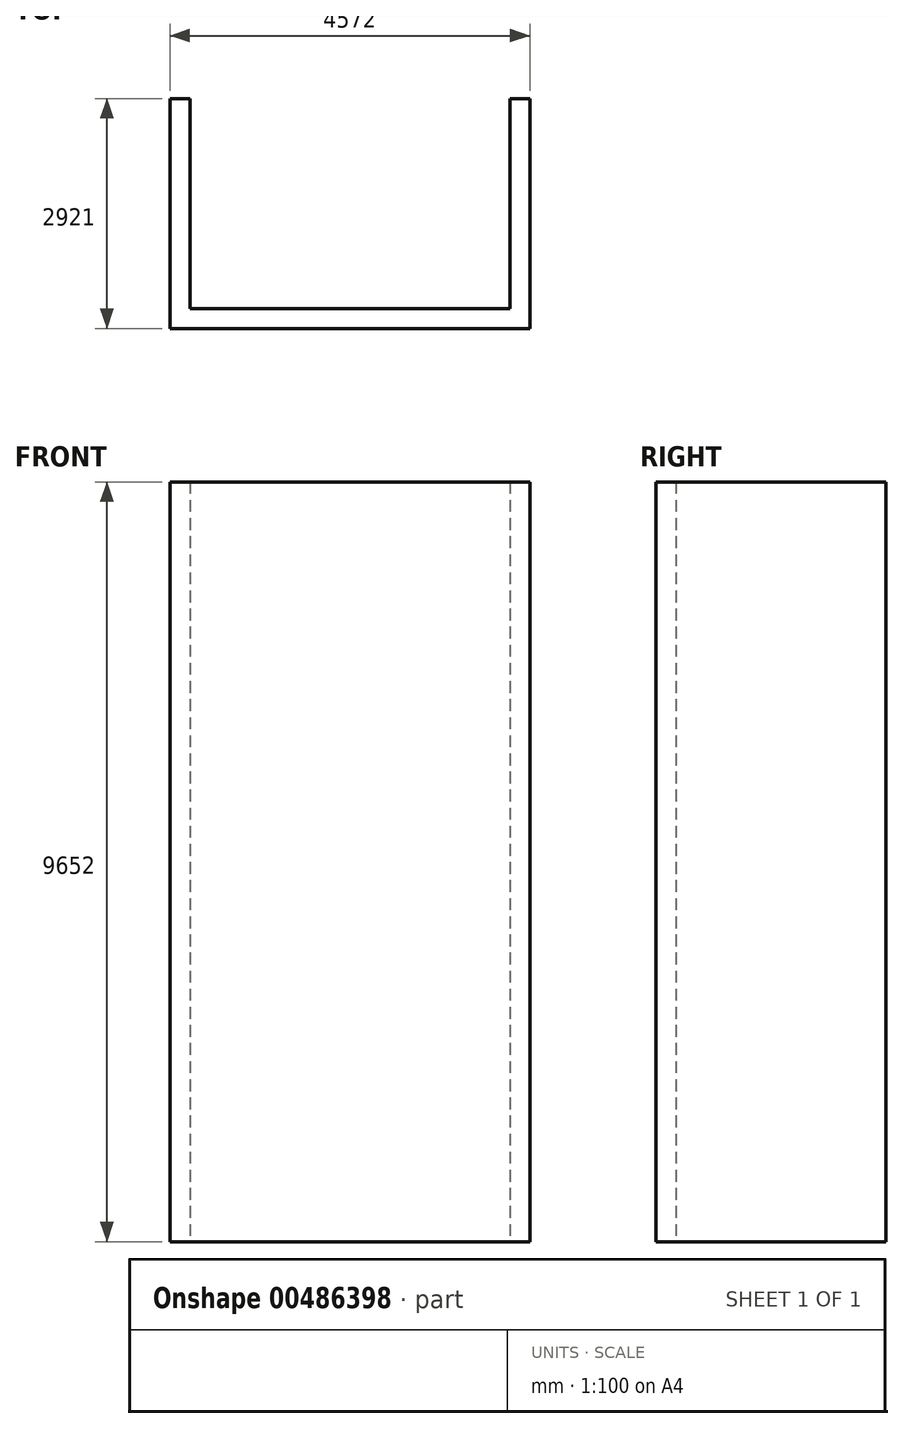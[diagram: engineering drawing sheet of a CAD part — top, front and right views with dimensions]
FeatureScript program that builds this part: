
annotation { "Feature Type Name" : "Feature", "Feature Type Description" : "" }
export const myFeature = defineFeature(function(context is Context, id is Id, definition is map)
    precondition{}
    {
        {
            var Q0;
            Q0=qCreatedBy(makeId("Top.planeOp"),FACE);
            var sketch = newSketch(context, id + "F0", { "sketchPlane" : qUnion([Q0])});
            skLineSegment(sketch, "E0", {"start": v(-2039.8, 0) * mm, "end": v(2532.2, 0) * mm});
            skLineSegment(sketch, "E1", {"start": v(2532.2, 0) * mm, "end": v(2532.2, 2921) * mm});
            skLineSegment(sketch, "E2", {"start": v(2532.2, 2921) * mm, "end": v(2278.2, 2921) * mm});
            skLineSegment(sketch, "E3", {"start": v(2278.2, 2921) * mm, "end": v(2278.2, 254) * mm});
            skLineSegment(sketch, "E4", {"start": v(2278.2, 254) * mm, "end": v(-1785.8, 254) * mm});
            skLineSegment(sketch, "E5", {"start": v(-1785.8, 254) * mm, "end": v(-1785.8, 2921) * mm});
            skLineSegment(sketch, "E6", {"start": v(-1785.8, 2921) * mm, "end": v(-2039.8, 2921) * mm});
            skLineSegment(sketch, "E7", {"start": v(-2039.8, 2921) * mm, "end": v(-2039.8, 0) * mm});
            skSolve(sketch);
        }
        {
            var Q0;
            Q0 = qSketchRegion(id + "F0", true);
            extrude(context, id + "F1", {"entities" : qUnion([Q0]), "endBound" : BoundingType.SYMMETRIC, "depth" : 9652 * mm});
        }
    });
